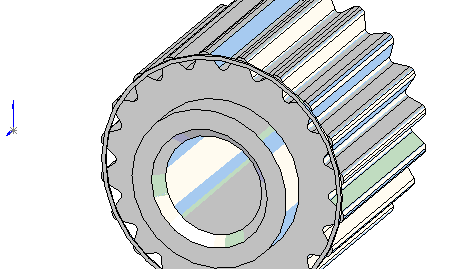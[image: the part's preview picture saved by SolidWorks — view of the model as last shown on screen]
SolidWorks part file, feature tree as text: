
SOLIDWORKS PART (.sldprt)
format: sldprt  version: not decoded by parser v0  size: 306,176 bytes
history: native  units: mm
features: material x3, plane x1, sketch x1, revolve x1, cut_extrude x1, fillet x1, pattern_circular x1, chamfer x1, extrude x1 + 5 further entries (+8 scaffold rows collapsed)
feature tree (24):
  scaffold x8  (default folders/planes/origin — collapsed)
  material  "Matériau <non spécifié>"
  material  "param"
  material  "param"
  "Corps de surface"
  plane  "Face"
  "Dessus"
  "Droite"
  sketch  "Esquisse1"
  revolve  "Révolution1"  Angle=360deg
  "Esquisse2"
  cut_extrude  "Enlèv. mat.-Extru.1"  [1 undecoded]
  fillet  "Congé1"  Radius=0.25mm
  pattern_circular  "Répétition circulaire1"  Count=20 Angle=360deg
  chamfer  "Chanfrein1"  Distance=0.5mm Angle=45deg
  "Esquisse3"
  extrude  "Extrusion1"  Depth=0.1mm
decode coverage: 5 of 7 modeling features carry decoded parameters; 5 rows unclassified (native names shown)
note: 1 parameter value undecoded
note: suppression state not decoded; provenance and decode notes live in map.json
